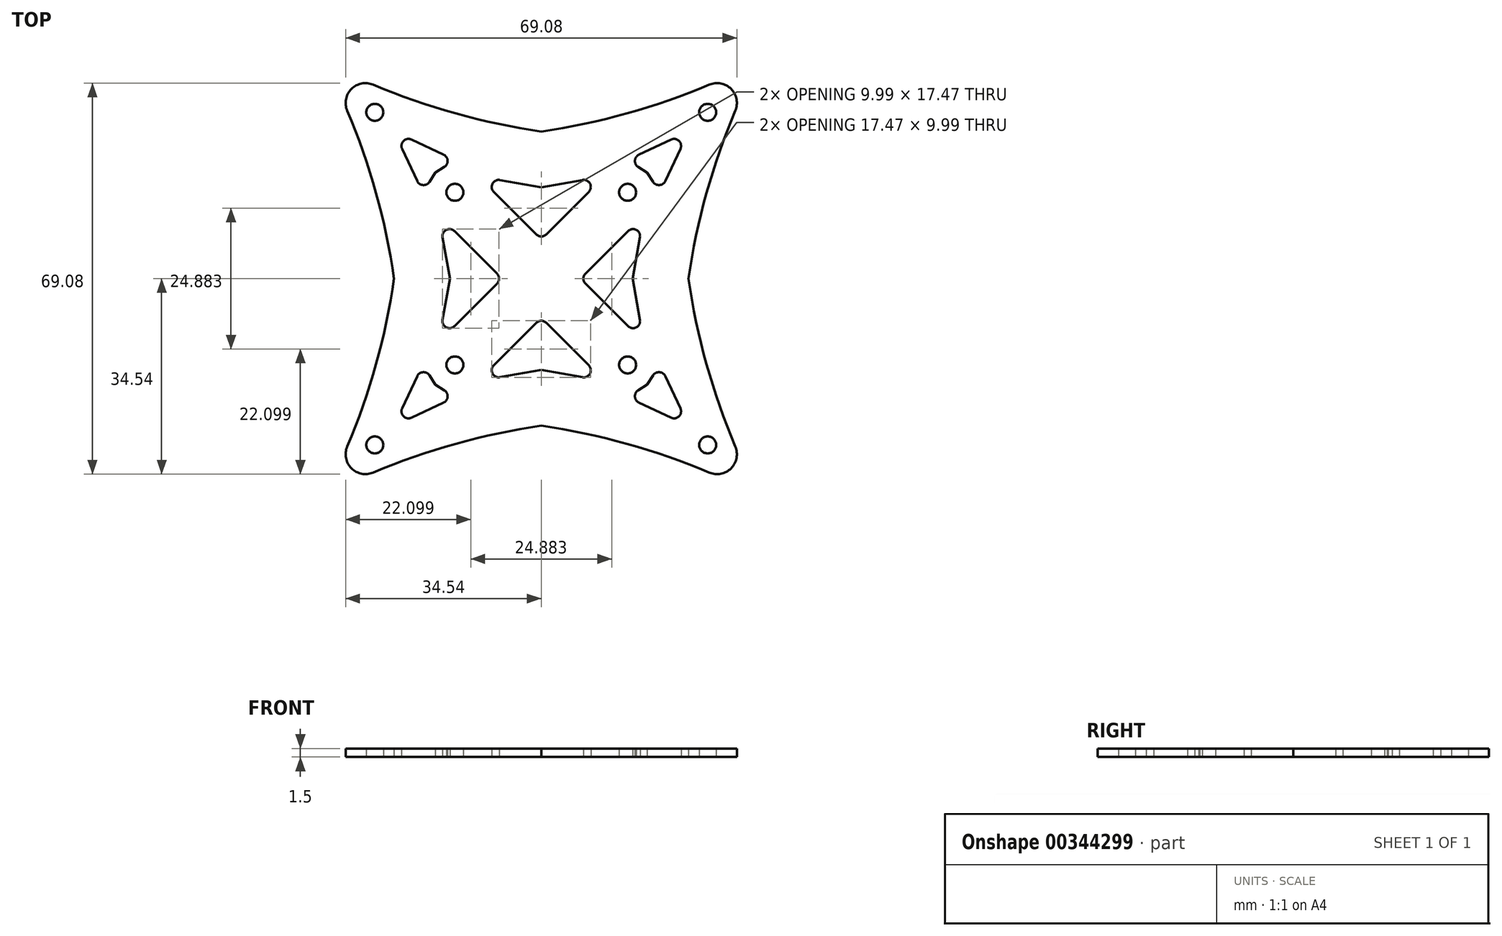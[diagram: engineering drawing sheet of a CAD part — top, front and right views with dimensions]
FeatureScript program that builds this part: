
annotation { "Feature Type Name" : "Feature", "Feature Type Description" : "" }
export const myFeature = defineFeature(function(context is Context, id is Id, definition is map)
    precondition{}
    {
        {
            var Q0;
            Q0=qCreatedBy(makeId("Top.planeOp"),FACE);
            var sketch = newSketch(context, id + "F0", { "sketchPlane" : qUnion([Q0])});
            skLineSegment(sketch, "E0", {"start": v(0, 114.28) * mm, "end": v(0, -108.92) * mm, "construction": true});
            skLineSegment(sketch, "E1", {"start": v(-111.96, 0) * mm, "end": v(120.54, 0) * mm, "construction": true});
            skLineSegment(sketch, "E2", {"start": v(0, 0) * mm, "end": v(98.63, 98.63) * mm, "construction": true});
            skLineSegment(sketch, "E3.0", {"start": v(7.81, 0.88) * mm, "end": v(15.31, 8.38) * mm});
            skCircle(sketch, "E4", {"center": v(15.25, 15.25) * mm, "radius": 1.5 * mm});
            skCircle(sketch, "E5", {"center": v(29.4, 29.4) * mm, "radius": 1.5 * mm});
            skPoint(sketch, "E6", {"position": v(33.52, 33.52) * mm});
            skArc(sketch, "E7", {"start": v(34.27, 29.68) * mm, "mid": v(34.48, 31.71) * mm, "end": v(33.52, 33.52) * mm});
            skLineSegment(sketch, "E8", {"start": v(34.41, 30.1) * mm, "end": v(26, 0) * mm, "construction": true});
            skArc(sketch, "E9", {"start": v(34.27, 29.68) * mm, "mid": v(29.18, 15.1) * mm, "end": v(26, 0) * mm});
            skLineSegment(sketch, "E10", {"start": v(16.13, 0) * mm, "end": v(17.43, 7.28) * mm});
            skArc(sketch, "E11", {"start": v(17.43, 7.28) * mm, "mid": v(16.78, 8.6) * mm, "end": v(15.31, 8.38) * mm});
            skLineSegment(sketch, "E12", {"start": v(18.7, 18.7) * mm, "end": v(19.74, 17.1) * mm});
            skArc(sketch, "E13", {"start": v(19.74, 17.1) * mm, "mid": v(20.87, 16.53) * mm, "end": v(21.92, 17.25) * mm});
            skArc(sketch, "E14", {"start": v(24.57, 22.9) * mm, "mid": v(24.67, 23.66) * mm, "end": v(24.32, 24.32) * mm});
            skLineSegment(sketch, "E15", {"start": v(21.92, 17.25) * mm, "end": v(24.57, 22.9) * mm});
            skArc(sketch, "E16.MirrorCS", {"start": v(29.68, 34.27) * mm, "mid": v(31.71, 34.48) * mm, "end": v(33.52, 33.52) * mm});
            skArc(sketch, "E17.MirrorCS", {"start": v(29.68, 34.27) * mm, "mid": v(15.1, 29.18) * mm, "end": v(0, 26) * mm});
            skArc(sketch, "E18.MirrorCS", {"start": v(22.9, 24.57) * mm, "mid": v(23.66, 24.67) * mm, "end": v(24.32, 24.32) * mm});
            skLineSegment(sketch, "E19.MirrorCS", {"start": v(17.25, 21.92) * mm, "end": v(22.9, 24.57) * mm});
            skArc(sketch, "E20.MirrorCS", {"start": v(17.1, 19.74) * mm, "mid": v(16.53, 20.87) * mm, "end": v(17.25, 21.92) * mm});
            skLineSegment(sketch, "E21.MirrorCS", {"start": v(18.7, 18.7) * mm, "end": v(17.1, 19.74) * mm});
            skLineSegment(sketch, "E22.MirrorCS", {"start": v(0, 16.13) * mm, "end": v(7.28, 17.43) * mm});
            skArc(sketch, "E23.MirrorCS", {"start": v(7.28, 17.43) * mm, "mid": v(8.6, 16.78) * mm, "end": v(8.38, 15.31) * mm});
            skLineSegment(sketch, "E24.MirrorCS", {"start": v(0.88, 7.81) * mm, "end": v(8.38, 15.31) * mm});
            skArc(sketch, "E25.MirrorCS", {"start": v(-17.1, 19.74) * mm, "mid": v(-16.53, 20.87) * mm, "end": v(-17.25, 21.92) * mm});
            skLineSegment(sketch, "E26.MirrorCS", {"start": v(-18.7, 18.7) * mm, "end": v(-19.74, 17.1) * mm});
            skArc(sketch, "E27.MirrorCS", {"start": v(-24.57, 22.9) * mm, "mid": v(-24.67, 23.66) * mm, "end": v(-24.32, 24.32) * mm});
            skArc(sketch, "E28.MirrorCS", {"start": v(-22.9, 24.57) * mm, "mid": v(-23.66, 24.67) * mm, "end": v(-24.32, 24.32) * mm});
            skLineSegment(sketch, "E29.MirrorCS", {"start": v(-18.7, 18.7) * mm, "end": v(-17.1, 19.74) * mm});
            skArc(sketch, "E30.MirrorCS", {"start": v(-19.74, 17.1) * mm, "mid": v(-20.87, 16.53) * mm, "end": v(-21.92, 17.25) * mm});
            skArc(sketch, "E31.MirrorCS", {"start": v(-7.28, 17.43) * mm, "mid": v(-8.6, 16.78) * mm, "end": v(-8.38, 15.31) * mm});
            skLineSegment(sketch, "E32.MirrorCS", {"start": v(-21.92, 17.25) * mm, "end": v(-24.57, 22.9) * mm});
            skArc(sketch, "E33.MirrorCS", {"start": v(-29.68, 34.27) * mm, "mid": v(-15.1, 29.18) * mm, "end": v(0, 26) * mm});
            skLineSegment(sketch, "E34.MirrorCS", {"start": v(-17.25, 21.92) * mm, "end": v(-22.9, 24.57) * mm});
            skLineSegment(sketch, "E35.MirrorCS", {"start": v(0, 16.13) * mm, "end": v(-7.28, 17.43) * mm});
            skArc(sketch, "E36.MirrorCS", {"start": v(-17.43, 7.28) * mm, "mid": v(-16.78, 8.6) * mm, "end": v(-15.31, 8.38) * mm});
            skLineSegment(sketch, "E37.MirrorCS", {"start": v(-16.13, 0) * mm, "end": v(-17.43, 7.28) * mm});
            skArc(sketch, "E38.MirrorCS", {"start": v(-34.27, 29.68) * mm, "mid": v(-29.18, 15.1) * mm, "end": v(-26, 0) * mm});
            skLineSegment(sketch, "E39.MirrorCS", {"start": v(-0.88, 7.81) * mm, "end": v(-8.38, 15.31) * mm});
            skArc(sketch, "E40.MirrorCS", {"start": v(-34.27, 29.68) * mm, "mid": v(-34.48, 31.71) * mm, "end": v(-33.52, 33.52) * mm});
            skArc(sketch, "E41.MirrorCS", {"start": v(-29.68, 34.27) * mm, "mid": v(-31.71, 34.48) * mm, "end": v(-33.52, 33.52) * mm});
            skCircle(sketch, "E42.MirrorC", {"center": v(-29.4, 29.4) * mm, "radius": 1.5 * mm});
            skLineSegment(sketch, "E43.MirrorCS", {"start": v(-7.81, 0.88) * mm, "end": v(-15.31, 8.38) * mm});
            skCircle(sketch, "E44.MirrorC", {"center": v(-15.25, 15.25) * mm, "radius": 1.5 * mm});
            skPoint(sketch, "E45.MirrorP", {"position": v(-33.52, 33.52) * mm});
            skArc(sketch, "E46.MirrorCS", {"start": v(24.57, -22.9) * mm, "mid": v(24.67, -23.66) * mm, "end": v(24.32, -24.32) * mm});
            skArc(sketch, "E47.MirrorCS", {"start": v(22.9, -24.57) * mm, "mid": v(23.66, -24.67) * mm, "end": v(24.32, -24.32) * mm});
            skArc(sketch, "E48.MirrorCS", {"start": v(-24.57, -22.9) * mm, "mid": v(-24.67, -23.66) * mm, "end": v(-24.32, -24.32) * mm});
            skArc(sketch, "E49.MirrorCS", {"start": v(17.1, -19.74) * mm, "mid": v(16.53, -20.87) * mm, "end": v(17.25, -21.92) * mm});
            skArc(sketch, "E50.MirrorCS", {"start": v(-17.43, -7.28) * mm, "mid": v(-16.78, -8.6) * mm, "end": v(-15.31, -8.38) * mm});
            skArc(sketch, "E51.MirrorCS", {"start": v(29.68, -34.27) * mm, "mid": v(31.71, -34.48) * mm, "end": v(33.52, -33.52) * mm});
            skArc(sketch, "E52.MirrorCS", {"start": v(34.27, -29.68) * mm, "mid": v(34.48, -31.71) * mm, "end": v(33.52, -33.52) * mm});
            skArc(sketch, "E53.MirrorCS", {"start": v(17.43, -7.28) * mm, "mid": v(16.78, -8.6) * mm, "end": v(15.31, -8.38) * mm});
            skLineSegment(sketch, "E54.MirrorCS", {"start": v(18.7, -18.7) * mm, "end": v(19.74, -17.1) * mm});
            skArc(sketch, "E55.MirrorCS", {"start": v(19.74, -17.1) * mm, "mid": v(20.87, -16.53) * mm, "end": v(21.92, -17.25) * mm});
            skArc(sketch, "E56.MirrorCS", {"start": v(-22.9, -24.57) * mm, "mid": v(-23.66, -24.67) * mm, "end": v(-24.32, -24.32) * mm});
            skArc(sketch, "E57.MirrorCS", {"start": v(-34.27, -29.68) * mm, "mid": v(-34.48, -31.71) * mm, "end": v(-33.52, -33.52) * mm});
            skArc(sketch, "E58.MirrorCS", {"start": v(7.28, -17.43) * mm, "mid": v(8.6, -16.78) * mm, "end": v(8.38, -15.31) * mm});
            skLineSegment(sketch, "E59.MirrorCS", {"start": v(18.7, -18.7) * mm, "end": v(17.1, -19.74) * mm});
            skArc(sketch, "E60.MirrorCS", {"start": v(-29.68, -34.27) * mm, "mid": v(-31.71, -34.48) * mm, "end": v(-33.52, -33.52) * mm});
            skArc(sketch, "E61.MirrorCS", {"start": v(-19.74, -17.1) * mm, "mid": v(-20.87, -16.53) * mm, "end": v(-21.92, -17.25) * mm});
            skLineSegment(sketch, "E62.MirrorCS", {"start": v(-18.7, -18.7) * mm, "end": v(-17.1, -19.74) * mm});
            skArc(sketch, "E63.MirrorCS", {"start": v(-7.28, -17.43) * mm, "mid": v(-8.6, -16.78) * mm, "end": v(-8.38, -15.31) * mm});
            skLineSegment(sketch, "E64.MirrorCS", {"start": v(-18.7, -18.7) * mm, "end": v(-19.74, -17.1) * mm});
            skArc(sketch, "E65.MirrorCS", {"start": v(-17.1, -19.74) * mm, "mid": v(-16.53, -20.87) * mm, "end": v(-17.25, -21.92) * mm});
            skLineSegment(sketch, "E66.MirrorCS", {"start": v(21.92, -17.25) * mm, "end": v(24.57, -22.9) * mm});
            skCircle(sketch, "E67.MirrorC", {"center": v(15.25, -15.25) * mm, "radius": 1.5 * mm});
            skLineSegment(sketch, "E68.MirrorCS", {"start": v(-7.81, -0.88) * mm, "end": v(-15.31, -8.38) * mm});
            skLineSegment(sketch, "E69.MirrorCS", {"start": v(7.81, -0.88) * mm, "end": v(15.31, -8.38) * mm});
            skCircle(sketch, "E70.MirrorC", {"center": v(29.4, -29.4) * mm, "radius": 1.5 * mm});
            skArc(sketch, "E71.MirrorCS", {"start": v(34.27, -29.68) * mm, "mid": v(29.18, -15.1) * mm, "end": v(26, 0) * mm});
            skLineSegment(sketch, "E72.MirrorCS", {"start": v(16.13, 0) * mm, "end": v(17.43, -7.28) * mm});
            skLineSegment(sketch, "E73.MirrorCS", {"start": v(17.25, -21.92) * mm, "end": v(22.9, -24.57) * mm});
            skCircle(sketch, "E74.MirrorC", {"center": v(-15.25, -15.25) * mm, "radius": 1.5 * mm});
            skLineSegment(sketch, "E75.MirrorCS", {"start": v(-17.25, -21.92) * mm, "end": v(-22.9, -24.57) * mm});
            skLineSegment(sketch, "E76.MirrorCS", {"start": v(0.88, -7.81) * mm, "end": v(8.38, -15.31) * mm});
            skLineSegment(sketch, "E77.MirrorCS", {"start": v(-0.88, -7.81) * mm, "end": v(-8.38, -15.31) * mm});
            skLineSegment(sketch, "E78.MirrorCS", {"start": v(-21.92, -17.25) * mm, "end": v(-24.57, -22.9) * mm});
            skArc(sketch, "E79.MirrorCS", {"start": v(29.68, -34.27) * mm, "mid": v(15.1, -29.18) * mm, "end": v(0, -26) * mm});
            skArc(sketch, "E80.MirrorCS", {"start": v(-34.27, -29.68) * mm, "mid": v(-29.18, -15.1) * mm, "end": v(-26, 0) * mm});
            skLineSegment(sketch, "E81.MirrorCS", {"start": v(-16.13, 0) * mm, "end": v(-17.43, -7.28) * mm});
            skPoint(sketch, "E82.MirrorP", {"position": v(-33.52, -33.52) * mm});
            skLineSegment(sketch, "E83.MirrorCS", {"start": v(0, -16.13) * mm, "end": v(7.28, -17.43) * mm});
            skLineSegment(sketch, "E84.MirrorCS", {"start": v(0, -16.13) * mm, "end": v(-7.28, -17.43) * mm});
            skCircle(sketch, "E85.MirrorC", {"center": v(-29.4, -29.4) * mm, "radius": 1.5 * mm});
            skPoint(sketch, "E86.MirrorP", {"position": v(33.52, -33.52) * mm});
            skArc(sketch, "E87.MirrorCS", {"start": v(-29.68, -34.27) * mm, "mid": v(-15.1, -29.18) * mm, "end": v(0, -26) * mm});
            skArc(sketch, "E88", {"start": v(7.81, 0.88) * mm, "mid": v(7.45, 0) * mm, "end": v(7.81, -0.88) * mm});
            skArc(sketch, "E89", {"start": v(-0.88, 7.81) * mm, "mid": v(0, 7.45) * mm, "end": v(0.88, 7.81) * mm});
            skArc(sketch, "E90", {"start": v(-7.81, -0.88) * mm, "mid": v(-7.45, 0) * mm, "end": v(-7.81, 0.88) * mm});
            skArc(sketch, "E91", {"start": v(0.88, -7.81) * mm, "mid": v(0, -7.45) * mm, "end": v(-0.88, -7.81) * mm});
            skPoint(sketch, "E92.orphan", {"position": v(6.93, 0) * mm});
            skPoint(sketch, "E93.orphan", {"position": v(0, -6.93) * mm});
            skPoint(sketch, "E94.orphan", {"position": v(-6.93, 0) * mm});
            skPoint(sketch, "E95.orphan", {"position": v(0, 6.93) * mm});
            skSolve(sketch);
        }
        {
            var Q0;
            Q0=makeQuery(id+"F0.imprint","IMPRINT",FACE,{"disambiguationData":[TD([[makeQuery(id+"F0.imprint","IMPRINT",EDGE,{"derivedFrom":sQuery(id+"F0.wireOp",EDGE,"E3.0")}),1.0]])]});
            extrude(context, id + "F1", {"entities" : qUnion([Q0]), "depth" : 1.5 * mm});
        }
    });
